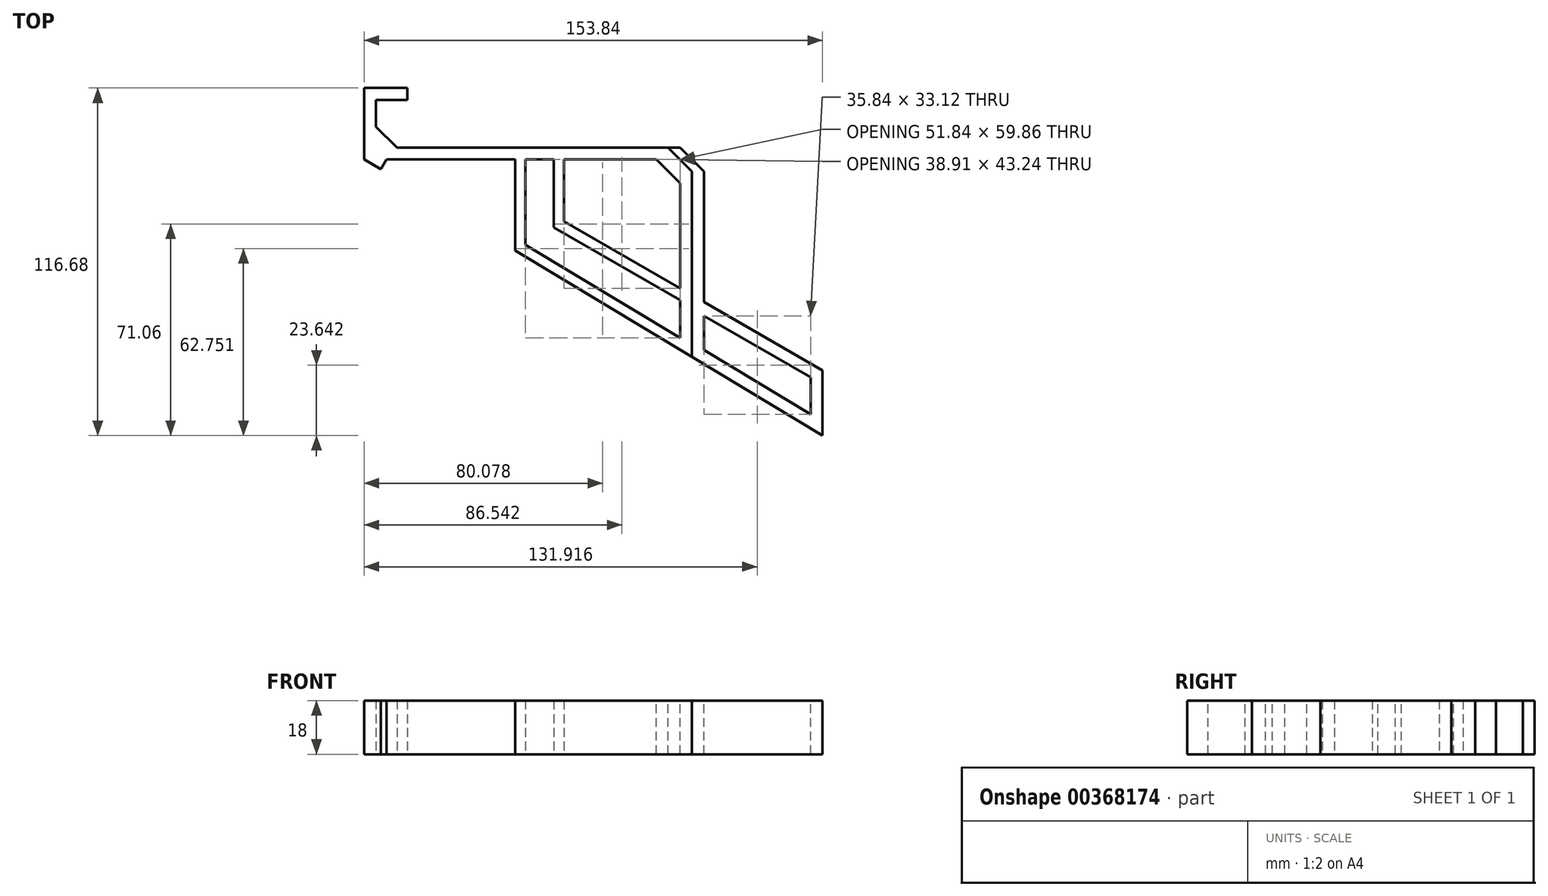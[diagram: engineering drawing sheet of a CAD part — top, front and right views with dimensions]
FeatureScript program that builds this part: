
annotation { "Feature Type Name" : "Feature", "Feature Type Description" : "" }
export const myFeature = defineFeature(function(context is Context, id is Id, definition is map)
    precondition{}
    {
        {
            var Q0;
            Q0=qCreatedBy(makeId("Top.planeOp"),FACE);
            var sketch = newSketch(context, id + "F0", { "sketchPlane" : qUnion([Q0])});
            skLineSegment(sketch, "E0", {"start": v(0, 16) * mm, "end": v(-10.43, 16) * mm});
            skLineSegment(sketch, "E1", {"start": v(-10.43, 16) * mm, "end": v(-10.43, 0) * mm});
            skLineSegment(sketch, "E2", {"start": v(-10.43, 0) * mm, "end": v(95.57, 0) * mm});
            skLineSegment(sketch, "E3.0", {"start": v(-14.43, -4) * mm, "end": v(95.57, -4) * mm});
            skLineSegment(sketch, "E3.1", {"start": v(-14.43, 20) * mm, "end": v(-14.43, -4) * mm});
            skLineSegment(sketch, "E3.2", {"start": v(0, 20) * mm, "end": v(-14.43, 20) * mm});
            skLineSegment(sketch, "E4", {"start": v(0, 16) * mm, "end": v(0, 20) * mm});
            skLineSegment(sketch, "E5", {"start": v(95.57, 0) * mm, "end": v(95.57, -4) * mm});
            skLineSegment(sketch, "E6", {"start": v(-10.43, 7) * mm, "end": v(-3.43, 0) * mm});
            skLineSegment(sketch, "E7", {"start": v(95.57, -4) * mm, "end": v(95.57, -70.27) * mm});
            skLineSegment(sketch, "E8", {"start": v(95.57, -70.27) * mm, "end": v(91.57, -67.86) * mm});
            skLineSegment(sketch, "E9", {"start": v(91.57, -67.86) * mm, "end": v(91.57, -4) * mm});
            skLineSegment(sketch, "E10", {"start": v(-14.43, -4) * mm, "end": v(95.57, -70.27) * mm, "construction": true});
            skSolve(sketch);
        }
        {
            var Q0;
            Q0=qSketchRegion(id+"F0",true);
            extrude(context, id + "F1", {"entities" : qUnion([Q0]), "depth" : 18 * mm, "symmetric" : true});
        }
        {
            var Q0;
            Q0=makeQuery(id+"F1.opExtrude","CAP_FACE",FACE,{"disambiguationData":[OSD([sQuery(id+"F0.wireOp",EDGE,"E0"),sQuery(id+"F0.wireOp",EDGE,"E1"),sQuery(id+"F0.wireOp",EDGE,"E2"),sQuery(id+"F0.wireOp",EDGE,"E3.0"),sQuery(id+"F0.wireOp",EDGE,"E3.1"),sQuery(id+"F0.wireOp",EDGE,"E3.2"),sQuery(id+"F0.wireOp",EDGE,"E4"),sQuery(id+"F0.wireOp",EDGE,"E5"),sQuery(id+"F0.wireOp",EDGE,"E6"),sQuery(id+"F0.wireOp",EDGE,"E7"),sQuery(id+"F0.wireOp",EDGE,"E8"),sQuery(id+"F0.wireOp",EDGE,"E9")])],"isStart":false});
            var sketch = newSketch(context, id + "F2", { "sketchPlane" : qUnion([Q0])});
            skLineSegment(sketch, "E11", {"start": v(95.57, -70.27) * mm, "end": v(-14.43, -4) * mm});
            skLineSegment(sketch, "E12", {"start": v(-14.43, -4) * mm, "end": v(-43.04, -4) * mm});
            skLineSegment(sketch, "E13", {"start": v(-43.04, -4) * mm, "end": v(-43.04, -70.27) * mm});
            skLineSegment(sketch, "E14", {"start": v(-43.04, -70.27) * mm, "end": v(95.57, -70.27) * mm});
            skSolve(sketch);
        }
        {
            var Q0;
            Q0=qSketchRegion(id+"F2",true);
            extrude(context, id + "F3", {"entities" : qUnion([Q0]), "operationType" : NewBodyOperationType.REMOVE, "oppositeDirection" : true, "depth" : 25 * mm});
        }
        {
            var Q0;
            Q0=makeQuery(id+"F1.opExtrude","CAP_FACE",FACE,{"disambiguationData":[OSD([sQuery(id+"F0.wireOp",EDGE,"E0"),sQuery(id+"F0.wireOp",EDGE,"E1"),sQuery(id+"F0.wireOp",EDGE,"E2"),sQuery(id+"F0.wireOp",EDGE,"E3.0"),sQuery(id+"F0.wireOp",EDGE,"E3.1"),sQuery(id+"F0.wireOp",EDGE,"E3.2"),sQuery(id+"F0.wireOp",EDGE,"E4"),sQuery(id+"F0.wireOp",EDGE,"E5"),sQuery(id+"F0.wireOp",EDGE,"E6"),sQuery(id+"F0.wireOp",EDGE,"E7"),sQuery(id+"F0.wireOp",EDGE,"E8"),sQuery(id+"F0.wireOp",EDGE,"E9")])],"isStart":false});
            var sketch = newSketch(context, id + "F4", { "sketchPlane" : qUnion([Q0])});
            skCircle(sketch, "E15.cCircle", {"center": v(91.57, -4) * mm, "radius": 63.86 * mm, "construction": true});
            skLineSegment(sketch, "E15.0", {"start": v(91.57, -67.86) * mm, "end": v(36.26, -35.93) * mm});
            skLineSegment(sketch, "E15.1", {"start": v(36.26, -35.93) * mm, "end": v(36.26, 27.93) * mm});
            skLineSegment(sketch, "E15.2", {"start": v(36.26, 27.93) * mm, "end": v(91.57, 59.86) * mm});
            skLineSegment(sketch, "E15.3", {"start": v(91.57, 59.86) * mm, "end": v(146.87, 27.93) * mm});
            skLineSegment(sketch, "E15.4", {"start": v(146.87, 27.93) * mm, "end": v(146.87, -35.93) * mm});
            skLineSegment(sketch, "E15.5", {"start": v(146.87, -35.93) * mm, "end": v(91.57, -67.86) * mm});
            skCircle(sketch, "E16.cCircle", {"center": v(91.57, -4) * mm, "radius": 59.86 * mm, "construction": true});
            skLineSegment(sketch, "E16.0", {"start": v(91.57, -63.86) * mm, "end": v(39.73, -33.93) * mm});
            skLineSegment(sketch, "E16.1", {"start": v(39.73, -33.93) * mm, "end": v(39.73, 25.93) * mm});
            skLineSegment(sketch, "E16.2", {"start": v(39.73, 25.93) * mm, "end": v(91.57, 55.86) * mm});
            skLineSegment(sketch, "E16.3", {"start": v(91.57, 55.86) * mm, "end": v(143.4, 25.93) * mm});
            skLineSegment(sketch, "E16.4", {"start": v(143.4, 25.93) * mm, "end": v(143.4, -33.93) * mm});
            skLineSegment(sketch, "E16.5", {"start": v(143.4, -33.93) * mm, "end": v(91.57, -63.86) * mm});
            skSolve(sketch);
        }
        {
            var Q0;
            Q0=qSketchRegion(id+"F4",true);
            extrude(context, id + "F5", {"entities" : qUnion([Q0]), "operationType" : NewBodyOperationType.ADD, "oppositeDirection" : true, "depth" : 18 * mm});
        }
        {
            var Q0;
            Q0=makeQuery(id+"F5.boolean.opBoolean","MERGE",FACE,{"derivedFrom":[makeQuery(id+"F1.opExtrude","CAP_FACE",FACE,{"disambiguationData":[OSD([sQuery(id+"F0.wireOp",EDGE,"E0"),sQuery(id+"F0.wireOp",EDGE,"E1"),sQuery(id+"F0.wireOp",EDGE,"E2"),sQuery(id+"F0.wireOp",EDGE,"E3.0"),sQuery(id+"F0.wireOp",EDGE,"E3.1"),sQuery(id+"F0.wireOp",EDGE,"E3.2"),sQuery(id+"F0.wireOp",EDGE,"E4"),sQuery(id+"F0.wireOp",EDGE,"E5"),sQuery(id+"F0.wireOp",EDGE,"E6"),sQuery(id+"F0.wireOp",EDGE,"E7"),sQuery(id+"F0.wireOp",EDGE,"E8"),sQuery(id+"F0.wireOp",EDGE,"E9")])],"isStart":false}),makeQuery(id+"F5.opExtrude","CAP_FACE",FACE,{"disambiguationData":[OSD([sQuery(id+"F4.wireOp",EDGE,"E15.0"),sQuery(id+"F4.wireOp",EDGE,"E15.1"),sQuery(id+"F4.wireOp",EDGE,"E15.2"),sQuery(id+"F4.wireOp",EDGE,"E15.3"),sQuery(id+"F4.wireOp",EDGE,"E15.4"),sQuery(id+"F4.wireOp",EDGE,"E15.5"),sQuery(id+"F4.wireOp",EDGE,"E16.0"),sQuery(id+"F4.wireOp",EDGE,"E16.1"),sQuery(id+"F4.wireOp",EDGE,"E16.2"),sQuery(id+"F4.wireOp",EDGE,"E16.3"),sQuery(id+"F4.wireOp",EDGE,"E16.4"),sQuery(id+"F4.wireOp",EDGE,"E16.5")])],"isStart":true})]});
            var sketch = newSketch(context, id + "F6", { "sketchPlane" : qUnion([Q0])});
            skCircle(sketch, "E17.cCircle", {"center": v(95.57, 0) * mm, "radius": 53.55 * mm, "construction": true});
            skLineSegment(sketch, "E17.0", {"start": v(95.57, -53.55) * mm, "end": v(49.2, -26.77) * mm});
            skLineSegment(sketch, "E17.1", {"start": v(49.2, -26.77) * mm, "end": v(49.2, 26.77) * mm});
            skLineSegment(sketch, "E17.2", {"start": v(49.2, 26.77) * mm, "end": v(95.57, 53.55) * mm});
            skLineSegment(sketch, "E17.3", {"start": v(95.57, 53.55) * mm, "end": v(141.94, 26.77) * mm});
            skLineSegment(sketch, "E17.4", {"start": v(141.94, 26.77) * mm, "end": v(141.94, -26.77) * mm});
            skLineSegment(sketch, "E17.5", {"start": v(141.94, -26.77) * mm, "end": v(95.57, -53.55) * mm});
            skCircle(sketch, "E18.cCircle", {"center": v(95.57, 0) * mm, "radius": 49.55 * mm, "construction": true});
            skLineSegment(sketch, "E18.0", {"start": v(95.57, -49.55) * mm, "end": v(52.66, -24.77) * mm});
            skLineSegment(sketch, "E18.1", {"start": v(52.66, -24.77) * mm, "end": v(52.66, 24.77) * mm});
            skLineSegment(sketch, "E18.2", {"start": v(52.66, 24.77) * mm, "end": v(95.57, 49.55) * mm});
            skLineSegment(sketch, "E18.3", {"start": v(95.57, 49.55) * mm, "end": v(138.48, 24.77) * mm});
            skLineSegment(sketch, "E18.4", {"start": v(138.48, 24.77) * mm, "end": v(138.48, -24.77) * mm});
            skLineSegment(sketch, "E18.5", {"start": v(138.48, -24.77) * mm, "end": v(95.57, -49.55) * mm});
            skSolve(sketch);
        }
        {
            var Q0;
            Q0=qSketchRegion(id+"F6",true);
            extrude(context, id + "F7", {"entities" : qUnion([Q0]), "operationType" : NewBodyOperationType.ADD, "oppositeDirection" : true, "depth" : 18 * mm});
        }
        {
            var Q0;
            Q0=makeQuery(id+"F1.opExtrude","SWEPT_EDGE",EDGE,{"disambiguationData":[OSD([sQuery(id+"F0.wireOp",EDGE,"E3.0"),sQuery(id+"F0.wireOp",EDGE,"E9")])]});
            chamfer(context, id + "F8", {"entities" : qUnion([Q0]), "width" : 8 * mm, "tangentPropagation" : true});
        }
        {
            var Q0;
            Q0=makeQuery(id+"F1.opExtrude","SWEPT_EDGE",EDGE,{"disambiguationData":[OSD([sQuery(id+"F0.wireOp",EDGE,"E2"),sQuery(id+"F0.wireOp",EDGE,"E5")])]});
            chamfer(context, id + "F9", {"entities" : qUnion([Q0]), "width" : 8 * mm, "tangentPropagation" : true});
        }
        {
            var Q0;
            Q0=makeQuery(id+"F7.boolean.opBoolean","MERGE",FACE,{"derivedFrom":[makeQuery(id+"F5.boolean.opBoolean","MERGE",FACE,{"derivedFrom":[makeQuery(id+"F1.opExtrude","CAP_FACE",FACE,{"disambiguationData":[OSD([sQuery(id+"F0.wireOp",EDGE,"E0"),sQuery(id+"F0.wireOp",EDGE,"E1"),sQuery(id+"F0.wireOp",EDGE,"E2"),sQuery(id+"F0.wireOp",EDGE,"E3.0"),sQuery(id+"F0.wireOp",EDGE,"E3.1"),sQuery(id+"F0.wireOp",EDGE,"E3.2"),sQuery(id+"F0.wireOp",EDGE,"E4"),sQuery(id+"F0.wireOp",EDGE,"E5"),sQuery(id+"F0.wireOp",EDGE,"E6"),sQuery(id+"F0.wireOp",EDGE,"E7"),sQuery(id+"F0.wireOp",EDGE,"E8"),sQuery(id+"F0.wireOp",EDGE,"E9")])],"isStart":false}),makeQuery(id+"F5.opExtrude","CAP_FACE",FACE,{"disambiguationData":[OSD([sQuery(id+"F4.wireOp",EDGE,"E15.0"),sQuery(id+"F4.wireOp",EDGE,"E15.1"),sQuery(id+"F4.wireOp",EDGE,"E15.2"),sQuery(id+"F4.wireOp",EDGE,"E15.3"),sQuery(id+"F4.wireOp",EDGE,"E15.4"),sQuery(id+"F4.wireOp",EDGE,"E15.5"),sQuery(id+"F4.wireOp",EDGE,"E16.0"),sQuery(id+"F4.wireOp",EDGE,"E16.1"),sQuery(id+"F4.wireOp",EDGE,"E16.2"),sQuery(id+"F4.wireOp",EDGE,"E16.3"),sQuery(id+"F4.wireOp",EDGE,"E16.4"),sQuery(id+"F4.wireOp",EDGE,"E16.5")])],"isStart":true})]}),makeQuery(id+"F7.opExtrude","CAP_FACE",FACE,{"disambiguationData":[OSD([sQuery(id+"F6.wireOp",EDGE,"E17.0"),sQuery(id+"F6.wireOp",EDGE,"E17.1"),sQuery(id+"F6.wireOp",EDGE,"E17.2"),sQuery(id+"F6.wireOp",EDGE,"E17.3"),sQuery(id+"F6.wireOp",EDGE,"E17.4"),sQuery(id+"F6.wireOp",EDGE,"E17.5"),sQuery(id+"F6.wireOp",EDGE,"E18.0"),sQuery(id+"F6.wireOp",EDGE,"E18.1"),sQuery(id+"F6.wireOp",EDGE,"E18.2"),sQuery(id+"F6.wireOp",EDGE,"E18.3"),sQuery(id+"F6.wireOp",EDGE,"E18.4"),sQuery(id+"F6.wireOp",EDGE,"E18.5")])],"isStart":true})]});
            var sketch = newSketch(context, id + "F10", { "sketchPlane" : qUnion([Q0])});
            skLineSegment(sketch, "E19", {"start": v(28.5, 0) * mm, "end": v(95.57, 0) * mm});
            skLineSegment(sketch, "E20", {"start": v(95.57, 0) * mm, "end": v(95.57, -73.17) * mm});
            skLineSegment(sketch, "E21", {"start": v(95.57, -73.17) * mm, "end": v(150.76, -38.64) * mm});
            skLineSegment(sketch, "E22", {"start": v(150.76, -38.64) * mm, "end": v(155.26, 64.33) * mm});
            skLineSegment(sketch, "E23", {"start": v(155.26, 64.33) * mm, "end": v(108.49, 79.65) * mm});
            skLineSegment(sketch, "E24", {"start": v(108.49, 79.65) * mm, "end": v(24.9, 40.95) * mm});
            skLineSegment(sketch, "E25", {"start": v(24.9, 40.95) * mm, "end": v(28.5, 0) * mm});
            skSolve(sketch);
        }
        {
            var Q0;
            Q0=qSketchRegion(id+"F10",true);
            extrude(context, id + "F11", {"entities" : qUnion([Q0]), "operationType" : NewBodyOperationType.REMOVE, "oppositeDirection" : true, "depth" : 25 * mm});
        }
        {
            var Q0;
            Q0=makeQuery(id+"F7.boolean.opBoolean","MERGE",FACE,{"derivedFrom":[makeQuery(id+"F5.boolean.opBoolean","MERGE",FACE,{"derivedFrom":[makeQuery(id+"F1.opExtrude","CAP_FACE",FACE,{"disambiguationData":[OSD([sQuery(id+"F0.wireOp",EDGE,"E0"),sQuery(id+"F0.wireOp",EDGE,"E1"),sQuery(id+"F0.wireOp",EDGE,"E2"),sQuery(id+"F0.wireOp",EDGE,"E3.0"),sQuery(id+"F0.wireOp",EDGE,"E3.1"),sQuery(id+"F0.wireOp",EDGE,"E3.2"),sQuery(id+"F0.wireOp",EDGE,"E4"),sQuery(id+"F0.wireOp",EDGE,"E5"),sQuery(id+"F0.wireOp",EDGE,"E6"),sQuery(id+"F0.wireOp",EDGE,"E7"),sQuery(id+"F0.wireOp",EDGE,"E8"),sQuery(id+"F0.wireOp",EDGE,"E9")])],"isStart":false}),makeQuery(id+"F5.opExtrude","CAP_FACE",FACE,{"disambiguationData":[OSD([sQuery(id+"F4.wireOp",EDGE,"E15.0"),sQuery(id+"F4.wireOp",EDGE,"E15.1"),sQuery(id+"F4.wireOp",EDGE,"E15.2"),sQuery(id+"F4.wireOp",EDGE,"E15.3"),sQuery(id+"F4.wireOp",EDGE,"E15.4"),sQuery(id+"F4.wireOp",EDGE,"E15.5"),sQuery(id+"F4.wireOp",EDGE,"E16.0"),sQuery(id+"F4.wireOp",EDGE,"E16.1"),sQuery(id+"F4.wireOp",EDGE,"E16.2"),sQuery(id+"F4.wireOp",EDGE,"E16.3"),sQuery(id+"F4.wireOp",EDGE,"E16.4"),sQuery(id+"F4.wireOp",EDGE,"E16.5")])],"isStart":true})]}),makeQuery(id+"F7.opExtrude","CAP_FACE",FACE,{"disambiguationData":[OSD([sQuery(id+"F6.wireOp",EDGE,"E17.0"),sQuery(id+"F6.wireOp",EDGE,"E17.1"),sQuery(id+"F6.wireOp",EDGE,"E17.2"),sQuery(id+"F6.wireOp",EDGE,"E17.3"),sQuery(id+"F6.wireOp",EDGE,"E17.4"),sQuery(id+"F6.wireOp",EDGE,"E17.5"),sQuery(id+"F6.wireOp",EDGE,"E18.0"),sQuery(id+"F6.wireOp",EDGE,"E18.1"),sQuery(id+"F6.wireOp",EDGE,"E18.2"),sQuery(id+"F6.wireOp",EDGE,"E18.3"),sQuery(id+"F6.wireOp",EDGE,"E18.4"),sQuery(id+"F6.wireOp",EDGE,"E18.5")])],"isStart":true})]});
            var sketch = newSketch(context, id + "F12", { "sketchPlane" : qUnion([Q0])});
            skLineSegment(sketch, "E26", {"start": v(-14.43, -4) * mm, "end": v(-8.84, -7.23) * mm});
            skLineSegment(sketch, "E27", {"start": v(-8.84, -7.23) * mm, "end": v(-6.97, -4) * mm});
            skLineSegment(sketch, "E28", {"start": v(-6.97, -4) * mm, "end": v(-14.43, -4) * mm});
            skSolve(sketch);
        }
        {
            var Q0;
            Q0=qSketchRegion(id+"F12",true);
            extrude(context, id + "F13", {"entities" : qUnion([Q0]), "operationType" : NewBodyOperationType.ADD, "oppositeDirection" : true, "depth" : 18 * mm});
        }
        {
            var Q0;
            Q0=makeQuery(id+"F13.boolean.opBoolean","MERGE",FACE,{"derivedFrom":[makeQuery(id+"F7.boolean.opBoolean","MERGE",FACE,{"derivedFrom":[makeQuery(id+"F5.boolean.opBoolean","MERGE",FACE,{"derivedFrom":[makeQuery(id+"F1.opExtrude","CAP_FACE",FACE,{"disambiguationData":[OSD([sQuery(id+"F0.wireOp",EDGE,"E0"),sQuery(id+"F0.wireOp",EDGE,"E1"),sQuery(id+"F0.wireOp",EDGE,"E2"),sQuery(id+"F0.wireOp",EDGE,"E3.0"),sQuery(id+"F0.wireOp",EDGE,"E3.1"),sQuery(id+"F0.wireOp",EDGE,"E3.2"),sQuery(id+"F0.wireOp",EDGE,"E4"),sQuery(id+"F0.wireOp",EDGE,"E5"),sQuery(id+"F0.wireOp",EDGE,"E6"),sQuery(id+"F0.wireOp",EDGE,"E7"),sQuery(id+"F0.wireOp",EDGE,"E8"),sQuery(id+"F0.wireOp",EDGE,"E9")])],"isStart":false}),makeQuery(id+"F5.opExtrude","CAP_FACE",FACE,{"disambiguationData":[OSD([sQuery(id+"F4.wireOp",EDGE,"E15.0"),sQuery(id+"F4.wireOp",EDGE,"E15.1"),sQuery(id+"F4.wireOp",EDGE,"E15.2"),sQuery(id+"F4.wireOp",EDGE,"E15.3"),sQuery(id+"F4.wireOp",EDGE,"E15.4"),sQuery(id+"F4.wireOp",EDGE,"E15.5"),sQuery(id+"F4.wireOp",EDGE,"E16.0"),sQuery(id+"F4.wireOp",EDGE,"E16.1"),sQuery(id+"F4.wireOp",EDGE,"E16.2"),sQuery(id+"F4.wireOp",EDGE,"E16.3"),sQuery(id+"F4.wireOp",EDGE,"E16.4"),sQuery(id+"F4.wireOp",EDGE,"E16.5")])],"isStart":true})]}),makeQuery(id+"F7.opExtrude","CAP_FACE",FACE,{"disambiguationData":[OSD([sQuery(id+"F6.wireOp",EDGE,"E17.0"),sQuery(id+"F6.wireOp",EDGE,"E17.1"),sQuery(id+"F6.wireOp",EDGE,"E17.2"),sQuery(id+"F6.wireOp",EDGE,"E17.3"),sQuery(id+"F6.wireOp",EDGE,"E17.4"),sQuery(id+"F6.wireOp",EDGE,"E17.5"),sQuery(id+"F6.wireOp",EDGE,"E18.0"),sQuery(id+"F6.wireOp",EDGE,"E18.1"),sQuery(id+"F6.wireOp",EDGE,"E18.2"),sQuery(id+"F6.wireOp",EDGE,"E18.3"),sQuery(id+"F6.wireOp",EDGE,"E18.4"),sQuery(id+"F6.wireOp",EDGE,"E18.5")])],"isStart":true})]}),makeQuery(id+"F13.opExtrude","CAP_FACE",FACE,{"disambiguationData":[OSD([sQuery(id+"F12.wireOp",EDGE,"E26"),sQuery(id+"F12.wireOp",EDGE,"E27"),sQuery(id+"F12.wireOp",EDGE,"E28")])],"isStart":true})]});
            var sketch = newSketch(context, id + "F14", { "sketchPlane" : qUnion([Q0])});
            skLineSegment(sketch, "E29", {"start": v(-14.43, -4) * mm, "end": v(95.57, -70.27) * mm});
            skLineSegment(sketch, "E30", {"start": v(95.57, -70.27) * mm, "end": v(95.57, -79.24) * mm});
            skLineSegment(sketch, "E31", {"start": v(95.57, -79.24) * mm, "end": v(-31.36, -4) * mm});
            skLineSegment(sketch, "E32", {"start": v(-31.36, -4) * mm, "end": v(-14.43, -4) * mm});
            skSolve(sketch);
        }
        {
            var Q0;
            Q0=qSketchRegion(id+"F14",true);
            extrude(context, id + "F15", {"entities" : qUnion([Q0]), "operationType" : NewBodyOperationType.REMOVE, "oppositeDirection" : true, "depth" : 25 * mm});
        }
        {
            var Q0;
            Q0=makeQuery(id+"F13.boolean.opBoolean","MERGE",FACE,{"derivedFrom":[makeQuery(id+"F7.boolean.opBoolean","MERGE",FACE,{"derivedFrom":[makeQuery(id+"F5.boolean.opBoolean","MERGE",FACE,{"derivedFrom":[makeQuery(id+"F1.opExtrude","CAP_FACE",FACE,{"disambiguationData":[OSD([sQuery(id+"F0.wireOp",EDGE,"E0"),sQuery(id+"F0.wireOp",EDGE,"E1"),sQuery(id+"F0.wireOp",EDGE,"E2"),sQuery(id+"F0.wireOp",EDGE,"E3.0"),sQuery(id+"F0.wireOp",EDGE,"E3.1"),sQuery(id+"F0.wireOp",EDGE,"E3.2"),sQuery(id+"F0.wireOp",EDGE,"E4"),sQuery(id+"F0.wireOp",EDGE,"E5"),sQuery(id+"F0.wireOp",EDGE,"E6"),sQuery(id+"F0.wireOp",EDGE,"E7"),sQuery(id+"F0.wireOp",EDGE,"E8"),sQuery(id+"F0.wireOp",EDGE,"E9")])],"isStart":false}),makeQuery(id+"F5.opExtrude","CAP_FACE",FACE,{"disambiguationData":[OSD([sQuery(id+"F4.wireOp",EDGE,"E15.0"),sQuery(id+"F4.wireOp",EDGE,"E15.1"),sQuery(id+"F4.wireOp",EDGE,"E15.2"),sQuery(id+"F4.wireOp",EDGE,"E15.3"),sQuery(id+"F4.wireOp",EDGE,"E15.4"),sQuery(id+"F4.wireOp",EDGE,"E15.5"),sQuery(id+"F4.wireOp",EDGE,"E16.0"),sQuery(id+"F4.wireOp",EDGE,"E16.1"),sQuery(id+"F4.wireOp",EDGE,"E16.2"),sQuery(id+"F4.wireOp",EDGE,"E16.3"),sQuery(id+"F4.wireOp",EDGE,"E16.4"),sQuery(id+"F4.wireOp",EDGE,"E16.5")])],"isStart":true})]}),makeQuery(id+"F7.opExtrude","CAP_FACE",FACE,{"disambiguationData":[OSD([sQuery(id+"F6.wireOp",EDGE,"E17.0"),sQuery(id+"F6.wireOp",EDGE,"E17.1"),sQuery(id+"F6.wireOp",EDGE,"E17.2"),sQuery(id+"F6.wireOp",EDGE,"E17.3"),sQuery(id+"F6.wireOp",EDGE,"E17.4"),sQuery(id+"F6.wireOp",EDGE,"E17.5"),sQuery(id+"F6.wireOp",EDGE,"E18.0"),sQuery(id+"F6.wireOp",EDGE,"E18.1"),sQuery(id+"F6.wireOp",EDGE,"E18.2"),sQuery(id+"F6.wireOp",EDGE,"E18.3"),sQuery(id+"F6.wireOp",EDGE,"E18.4"),sQuery(id+"F6.wireOp",EDGE,"E18.5")])],"isStart":true})]}),makeQuery(id+"F13.opExtrude","CAP_FACE",FACE,{"disambiguationData":[OSD([sQuery(id+"F12.wireOp",EDGE,"E26"),sQuery(id+"F12.wireOp",EDGE,"E27"),sQuery(id+"F12.wireOp",EDGE,"E28")])],"isStart":true})]});
            var sketch = newSketch(context, id + "F16", { "sketchPlane" : qUnion([Q0])});
            skLineSegment(sketch, "E33", {"start": v(91.57, -63.86) * mm, "end": v(39.73, -32.63) * mm});
            skLineSegment(sketch, "E34", {"start": v(39.73, -32.63) * mm, "end": v(36.26, -34.54) * mm});
            skLineSegment(sketch, "E35", {"start": v(36.26, -34.54) * mm, "end": v(91.57, -67.86) * mm});
            skLineSegment(sketch, "E36", {"start": v(91.57, -67.86) * mm, "end": v(91.57, -63.86) * mm});
            skSolve(sketch);
        }
        {
            var Q0;
            Q0=qSketchRegion(id+"F16",true);
            extrude(context, id + "F17", {"entities" : qUnion([Q0]), "operationType" : NewBodyOperationType.ADD, "oppositeDirection" : true, "depth" : 18 * mm});
        }
        {
            var Q0;
            Q0=makeQuery(id+"F17.boolean.opBoolean","MERGE",FACE,{"derivedFrom":[makeQuery(id+"F13.boolean.opBoolean","MERGE",FACE,{"derivedFrom":[makeQuery(id+"F7.boolean.opBoolean","MERGE",FACE,{"derivedFrom":[makeQuery(id+"F5.boolean.opBoolean","MERGE",FACE,{"derivedFrom":[makeQuery(id+"F1.opExtrude","CAP_FACE",FACE,{"disambiguationData":[OSD([sQuery(id+"F0.wireOp",EDGE,"E0"),sQuery(id+"F0.wireOp",EDGE,"E1"),sQuery(id+"F0.wireOp",EDGE,"E2"),sQuery(id+"F0.wireOp",EDGE,"E3.0"),sQuery(id+"F0.wireOp",EDGE,"E3.1"),sQuery(id+"F0.wireOp",EDGE,"E3.2"),sQuery(id+"F0.wireOp",EDGE,"E4"),sQuery(id+"F0.wireOp",EDGE,"E5"),sQuery(id+"F0.wireOp",EDGE,"E6"),sQuery(id+"F0.wireOp",EDGE,"E7"),sQuery(id+"F0.wireOp",EDGE,"E8"),sQuery(id+"F0.wireOp",EDGE,"E9")])],"isStart":false}),makeQuery(id+"F5.opExtrude","CAP_FACE",FACE,{"disambiguationData":[OSD([sQuery(id+"F4.wireOp",EDGE,"E15.0"),sQuery(id+"F4.wireOp",EDGE,"E15.1"),sQuery(id+"F4.wireOp",EDGE,"E15.2"),sQuery(id+"F4.wireOp",EDGE,"E15.3"),sQuery(id+"F4.wireOp",EDGE,"E15.4"),sQuery(id+"F4.wireOp",EDGE,"E15.5"),sQuery(id+"F4.wireOp",EDGE,"E16.0"),sQuery(id+"F4.wireOp",EDGE,"E16.1"),sQuery(id+"F4.wireOp",EDGE,"E16.2"),sQuery(id+"F4.wireOp",EDGE,"E16.3"),sQuery(id+"F4.wireOp",EDGE,"E16.4"),sQuery(id+"F4.wireOp",EDGE,"E16.5")])],"isStart":true})]}),makeQuery(id+"F7.opExtrude","CAP_FACE",FACE,{"disambiguationData":[OSD([sQuery(id+"F6.wireOp",EDGE,"E17.0"),sQuery(id+"F6.wireOp",EDGE,"E17.1"),sQuery(id+"F6.wireOp",EDGE,"E17.2"),sQuery(id+"F6.wireOp",EDGE,"E17.3"),sQuery(id+"F6.wireOp",EDGE,"E17.4"),sQuery(id+"F6.wireOp",EDGE,"E17.5"),sQuery(id+"F6.wireOp",EDGE,"E18.0"),sQuery(id+"F6.wireOp",EDGE,"E18.1"),sQuery(id+"F6.wireOp",EDGE,"E18.2"),sQuery(id+"F6.wireOp",EDGE,"E18.3"),sQuery(id+"F6.wireOp",EDGE,"E18.4"),sQuery(id+"F6.wireOp",EDGE,"E18.5")])],"isStart":true})]}),makeQuery(id+"F13.opExtrude","CAP_FACE",FACE,{"disambiguationData":[OSD([sQuery(id+"F12.wireOp",EDGE,"E26"),sQuery(id+"F12.wireOp",EDGE,"E27"),sQuery(id+"F12.wireOp",EDGE,"E28")])],"isStart":true})]}),makeQuery(id+"F17.opExtrude","CAP_FACE",FACE,{"disambiguationData":[OSD([sQuery(id+"F16.wireOp",EDGE,"E33"),sQuery(id+"F16.wireOp",EDGE,"E34"),sQuery(id+"F16.wireOp",EDGE,"E35"),sQuery(id+"F16.wireOp",EDGE,"E36")])],"isStart":true})]});
            var sketch = newSketch(context, id + "F18", { "sketchPlane" : qUnion([Q0])});
            skLineSegment(sketch, "E37", {"start": v(95.57, -70.27) * mm, "end": v(139.4, -96.68) * mm});
            skLineSegment(sketch, "E38", {"start": v(139.4, -96.68) * mm, "end": v(139.4, -92) * mm});
            skLineSegment(sketch, "E39", {"start": v(139.4, -92) * mm, "end": v(95.57, -65.6) * mm});
            skLineSegment(sketch, "E40", {"start": v(95.57, -65.6) * mm, "end": v(95.57, -8) * mm});
            skLineSegment(sketch, "E41", {"start": v(95.57, -8) * mm, "end": v(87.57, 0) * mm});
            skLineSegment(sketch, "E42", {"start": v(87.57, 0) * mm, "end": v(91.57, 0) * mm});
            skLineSegment(sketch, "E43", {"start": v(91.57, 0) * mm, "end": v(99.57, -8) * mm});
            skLineSegment(sketch, "E44", {"start": v(99.57, -8) * mm, "end": v(99.57, -68) * mm});
            skLineSegment(sketch, "E45", {"start": v(95.57, -70.27) * mm, "end": v(95.57, -65.6) * mm});
            skLineSegment(sketch, "E46", {"start": v(95.57, -49.55) * mm, "end": v(139.4, -74.86) * mm});
            skLineSegment(sketch, "E47", {"start": v(139.4, -74.86) * mm, "end": v(139.4, -79.48) * mm});
            skLineSegment(sketch, "E48", {"start": v(139.4, -79.48) * mm, "end": v(95.57, -54.17) * mm});
            skLineSegment(sketch, "E49", {"start": v(95.57, -54.17) * mm, "end": v(95.57, -49.55) * mm});
            skLineSegment(sketch, "E50", {"start": v(75.35, -37.88) * mm, "end": v(131.48, -70.28) * mm});
            skLineSegment(sketch, "E51", {"start": v(139.4, -92) * mm, "end": v(139.4, -79.48) * mm});
            skLineSegment(sketch, "E52", {"start": v(135.4, -89.6) * mm, "end": v(135.4, -77.17) * mm});
            skSolve(sketch);
        }
        {
            var Q0;
            Q0=qSketchRegion(id+"F18",true);
            extrude(context, id + "F19", {"entities" : qUnion([Q0]), "oppositeDirection" : true, "depth" : 18 * mm});
        }
    });
